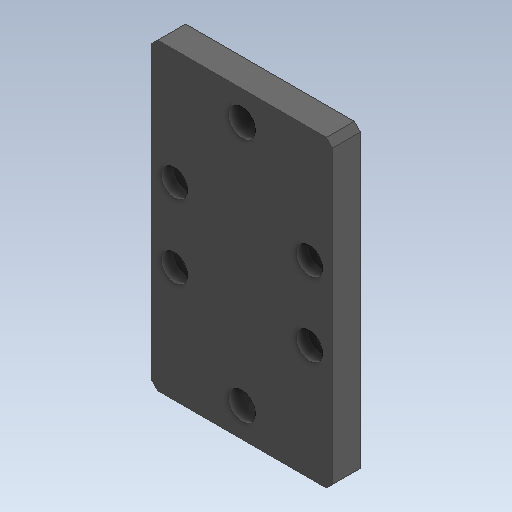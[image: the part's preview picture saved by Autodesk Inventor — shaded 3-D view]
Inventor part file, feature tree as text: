
AUTODESK INVENTOR PART (.ipt)
format: ipt  version: 2020.4 (Build 244396000, 396)  size: 180,224 bytes
history: native  units: in
note: dims shown in document units (in); Inventor stores cm internally (conversion verified against a paired STEP export)
features: sketch x5, hole x3, extrude x2, chamfer x1
ambient origin geometry x8: Origin, YZ Plane, XZ Plane, XY Plane, X Axis, Y Axis, Z Axis, Center Point
bodies: Solid1 (feature_tree)
feature tree (11):
  extrude  "Extrusion1"  Depth=0.0827in
  extrude  "Extrusion2"  TaperAngle=0.0deg  [1 undecoded]
  hole  "Hole1"  [1 undecoded]
  hole  "Hole3"  [1 undecoded]
  hole  "Hole6"  [1 undecoded]
  chamfer  "Chamfer3"  Distance=1.1614in
  sketch  "Sketch1"  dims[d2=0.1791in d3=0.0in]
  sketch  "Sketch2"  dims[d4=0.0945in d5=0.5in d6=0.1732in d7=0.0827in d8=90.0deg d9=0.75in d10=0.0in d11=0.8661in]
  sketch  "Sketch4"  dims[d12=0.0in d13=0.0in]
  sketch  "Sketch5"  dims[d14=0.0in d15=0.0in]
  sketch  "Sketch9"  dims[d16=0.4724in d17=0.2362in d18=0.4331in d30=1.1614in d31=0.1791in d32=0.0in d33=0.1772in d34=0.198in d35=0.3126in d36=0.1642in d37=90.0deg d38=0.75in d39=0.0in d40=0.0in d41=0.0in d42=0.7874in d43=1.5748in d72=0.1476in d73=0.198in d74=0.3126in d75=0.1642in d76=90.0deg d77=0.0197in d78=0.0in d79=0.0in d80=0.0in d81=0.0in d82=0.4724in d83=0.0in d84=0.8661in d85=0.0in d86=0.0in d87=0.0394in d88=0.0787in d89=45.0deg d54=0.0394in d55=0.0394in d56=0.0394in d57=0.0059in d58=0.0098in d59=0.0148in d60=0.5635in d61=0.0295in d62=0.8108in d63=0.0025in d64=0.0295in d65=0.0148in d90=0.0059in d91=0.0098in d92=0.0148in d93=0.5635in d94=0.0295in d95=0.8108in d96=0.0025in d97=0.0295in d98=0.0148in d99=0.0025in d100=0.0295in d101=0.0148in]
note: 4 required parameter values undecoded (feature->parameter linkage not recoverable at this tier; creation-order binding heuristic only, values carry confidence <= 0.55)
